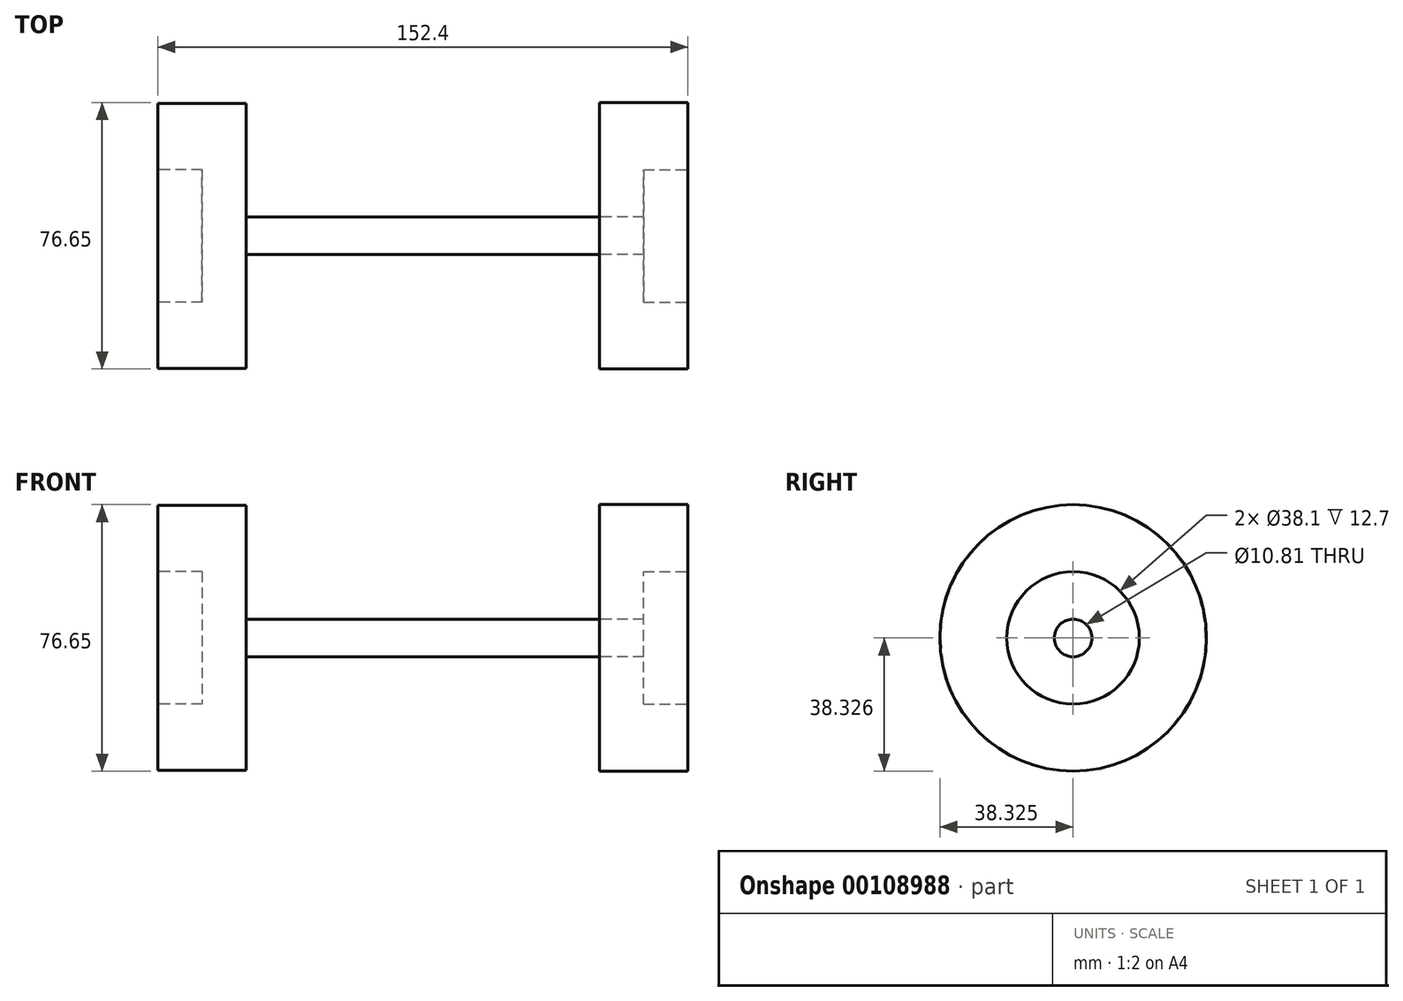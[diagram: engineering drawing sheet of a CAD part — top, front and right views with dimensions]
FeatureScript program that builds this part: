
annotation { "Feature Type Name" : "Feature", "Feature Type Description" : "" }
export const myFeature = defineFeature(function(context is Context, id is Id, definition is map)
    precondition{}
    {
        {
            var Q0;
            Q0=qCreatedBy(makeId("Right.planeOp"),FACE);
            var sketch = newSketch(context, id + "F0", { "sketchPlane" : qUnion([Q0])});
            skCircle(sketch, "E0", {"center": v(-57.63, 52.25) * mm, "radius": 38.1 * mm});
            skSolve(sketch);
        }
        {
            var Q0;
            Q0=makeQuery(id+"F0.imprint","IMPRINT",FACE,{"disambiguationData":[TD([[makeQuery(id+"F0.imprint","IMPRINT",EDGE,{"derivedFrom":sQuery(id+"F0.wireOp",EDGE,"E0")}),1.0]])]});
            extrude(context, id + "F1", {"entities" : qUnion([Q0]), "depth" : 25.4 * mm});
        }
        {
            var Q0;
            Q0=makeQuery(id+"F1.opExtrude","CAP_FACE",FACE,{"disambiguationData":[OSD([sQuery(id+"F0.wireOp",EDGE,"E0")])],"isStart":false});
            var sketch = newSketch(context, id + "F2", { "sketchPlane" : qUnion([Q0])});
            skCircle(sketch, "E1", {"center": v(-57.63, 52.25) * mm, "radius": 5.4 * mm});
            skSolve(sketch);
        }
        {
            var Q0;
            Q0=makeQuery(id+"F2.imprint","IMPRINT",FACE,{"disambiguationData":[TD([[makeQuery(id+"F2.imprint","IMPRINT",EDGE,{"derivedFrom":sQuery(id+"F2.wireOp",EDGE,"E1")}),1.0]])]});
            extrude(context, id + "F3", {"entities" : qUnion([Q0]), "operationType" : NewBodyOperationType.ADD, "depth" : 101.6 * mm});
        }
        {
            var Q0;
            Q0=makeQuery(id+"F3.opExtrude","CAP_FACE",FACE,{"disambiguationData":[OSD([sQuery(id+"F2.wireOp",EDGE,"E1")])],"isStart":false});
            var sketch = newSketch(context, id + "F4", { "sketchPlane" : qUnion([Q0])});
            skCircle(sketch, "E2", {"center": v(-57.63, 52.25) * mm, "radius": 38.32 * mm});
            skSolve(sketch);
        }
        {
            var Q0;
            Q0=makeQuery(id+"F4.imprint","IMPRINT",FACE,{"disambiguationData":[TD([[makeQuery(id+"F4.imprint","IMPRINT",EDGE,{"derivedFrom":sQuery(id+"F4.wireOp",EDGE,"E2")}),1.0]])]});
            extrude(context, id + "F5", {"entities" : qUnion([Q0]), "depth" : 25.4 * mm});
        }
        {
            var Q0;
            Q0=makeQuery(id+"F1.opExtrude","CAP_FACE",FACE,{"disambiguationData":[OSD([sQuery(id+"F0.wireOp",EDGE,"E0")])],"isStart":true});
            var sketch = newSketch(context, id + "F6", { "sketchPlane" : qUnion([Q0])});
            skCircle(sketch, "E3", {"center": v(57.63, 52.25) * mm, "radius": 19.05 * mm});
            skSolve(sketch);
        }
        {
            var Q0;
            Q0=makeQuery(id+"F6.imprint","IMPRINT",FACE,{"disambiguationData":[TD([[makeQuery(id+"F6.imprint","IMPRINT",EDGE,{"derivedFrom":sQuery(id+"F6.wireOp",EDGE,"E3")}),1.0]])]});
            extrude(context, id + "F7", {"entities" : qUnion([Q0]), "operationType" : NewBodyOperationType.REMOVE, "oppositeDirection" : true, "depth" : 12.7 * mm});
        }
        {
            var Q0;
            Q0=makeQuery(id+"F5.opExtrude","CAP_FACE",FACE,{"disambiguationData":[OSD([sQuery(id+"F2.wireOp",EDGE,"E1"),sQuery(id+"F4.wireOp",EDGE,"E2")])],"isStart":false});
            var sketch = newSketch(context, id + "F8", { "sketchPlane" : qUnion([Q0])});
            skCircle(sketch, "E4", {"center": v(-57.63, 52.25) * mm, "radius": 19.05 * mm});
            skSolve(sketch);
        }
        {
            var Q0;
            Q0=makeQuery(id+"F8.imprint","IMPRINT",FACE,{"disambiguationData":[TD([[makeQuery(id+"F8.imprint","IMPRINT",EDGE,{"derivedFrom":sQuery(id+"F8.wireOp",EDGE,"E4")}),1.0]])]});
            extrude(context, id + "F9", {"entities" : qUnion([Q0]), "operationType" : NewBodyOperationType.REMOVE, "oppositeDirection" : true, "depth" : 12.7 * mm});
        }
        {
            var Q0;
            Q0=makeQuery(id+"F1.opExtrude","CAP_FACE",FACE,{"disambiguationData":[OSD([sQuery(id+"F0.wireOp",EDGE,"E0")])],"isStart":true});
            var sketch = newSketch(context, id + "F10", { "sketchPlane" : qUnion([Q0])});
            skSolve(sketch);
        }
        {
            var Q0;
            Q0=makeQuery(id+"F10.imprint","IMPRINT",FACE,{"disambiguationData":[TD([[makeQuery(id+"F10.imprint","IMPRINT",EDGE,{"derivedFrom":makeQuery(id+"F1.opExtrude","CAP_EDGE",EDGE,{"disambiguationData":[OSD([sQuery(id+"F0.wireOp",EDGE,"E0")])],"isStart":true})}),-1.0]])]});
            var sketch = newSketch(context, id + "F11", { "sketchPlane" : qUnion([Q0])});
            skCircle(sketch, "E5", {"center": v(62.17, 37.4) * mm, "radius": 2.85 * mm});
            skCircle(sketch, "E6", {"center": v(51.6, 37.4) * mm, "radius": 2.85 * mm});
            skCircle(sketch, "E7", {"center": v(44.55, 45.95) * mm, "radius": 3.18 * mm});
            skCircle(sketch, "E8", {"center": v(44.55, 56.02) * mm, "radius": 3.06 * mm});
            skCircle(sketch, "E9", {"center": v(52.1, 63.07) * mm, "radius": 3.22 * mm});
            skCircle(sketch, "E10", {"center": v(62.17, 63.57) * mm, "radius": 3.63 * mm});
            skCircle(sketch, "E11", {"center": v(70.22, 56.53) * mm, "radius": 3.52 * mm});
            skCircle(sketch, "E12", {"center": v(70.22, 44.95) * mm, "radius": 3.22 * mm});
            skSolve(sketch);
        }
        {
            var Q0;
            Q0 = qSketchRegion(id + "F11", true);
            extrude(context, id + "F12", {"entities" : qUnion([Q0]), "operationType" : NewBodyOperationType.REMOVE, "oppositeDirection" : true, "depth" : 12.7 * mm});
        }
    });
